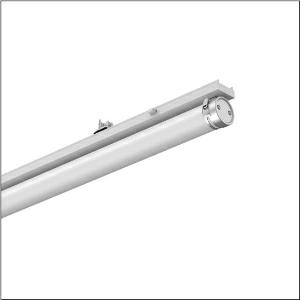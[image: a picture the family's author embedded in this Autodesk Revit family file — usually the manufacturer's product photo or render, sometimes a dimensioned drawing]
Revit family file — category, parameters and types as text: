
# Revit family: monsun_r__31_tube_51ft10nn4a0atr1_e6cc
name_source: partatom
category: Lighting Fixtures
units: mm (PartAtom-declared; Revit-internal decimal feet)

## family parameters
Cut with Voids When Loaded = No
Host = Face
Light Source = No
Part Type = Normal
Room Calculation Point = No
Round Connector Dimension = Use Diameter
Shared = No

## types (1)
- --- (1 x LED, 10000 lm, 58 W, 4000K)
    Apparent Load = 58 VA
    CIE Flux Codes = 42 71 90 91 100
    Color Rendering = 80
    Color Temperature = 4000K
    Default Elevation = 1800 mm
    Description = Monsun® 31 Tube, tubular luminaire, primary optical cover: diffuser, of PMMA, light emission: direct distribution, primary light characteristic: symmetric, LED, rated luminous flux: 10.000lm, luminous efficacy: 172lm/W, light colour: 840, colour temperature: 4000K, with with 1 terminal, 5-pole, max. 2.5mm², mains connection: 220..240V, AC, 50/60Hz, rated input power: 58W, housing, cylindrical, of PMMA, semi-transparent, matt white, with luminaire and ceiling fastening, V4A, mounting with brackets of stainless steel, length: 1.495mm, diameter: 75mm, end cap, of stainless steel (V4A), protection rating (complete): IP20, protection rating (lamp compartment): IP67/69K, insulation class (complete): insulation class I (protective earthing), certification: CE, UKCA, impact resistance: IK07, permissible operating ambient temperature: -20..+40°C, corresponds to IFS (International Featured Standards) requirements for safety and quality in the food industry, contact your sales advisor before using the luminaires in applications with unclear chemical exposure, large temperature fluctuations or condensation-forming humidity, packaging unit: 1 piece
    Height = 118 mm
    Lamp = 1 x LED
    Lamp Light Flux = 10000 lm
    Lamp Power = 58 W
    Lamp count = 1
    Length = 1495 mm
    Luminous efficacy = 172 lm/W
    Manufacturer = Siteco
    ModVariant = No
    Model = 51FT10NN4A0ATR1
    Mounting Place = Ceiling
    Mounting Type = Pendant
    Number of Poles = 1
    OnlyDefault = Yes
    Power Factor = 1
    Product Name = Monsun® 31 Tube
    Product group = tubular luminaire
    ProductGroupID = 906
    Protection Class = Protection class I
    Protection Degree = IP 20
    RLX_Detail_Level = 1
    RLX_Emergency_Light_Flux = 0 lm
    RLX_Emergency_Type = 0
    RLX_Emergency_Type_DB = No
    RlxData = <blob elided: 32369 chars, md5=0d6e8b68>
    Socket = socket
    Standby Power = 0 W
    System Light Flux = 10000 lm
    System Power = 58 W
    Type Comments = individual setting: luminous flux: 100 % | (OFF | OFF | ON | OFF) | 350 mA
    Type Image = l_1007227.jpg
    URL = http://relux.com
    VarID = @adj_074695
    Voltage = 0 V
    Weight = 0.00 kg
    Width = 75 mm

## geometry (parser evidence)
native form markers: Blend x4, Sweep x10
no freeform markers — native parametric forms only
